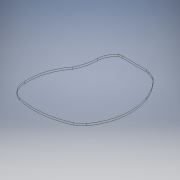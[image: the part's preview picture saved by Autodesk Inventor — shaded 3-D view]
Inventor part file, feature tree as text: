
AUTODESK INVENTOR PART (.ipt)
format: ipt  version: 2018 (Build 220112000, 112)  size: 170,496 bytes
history: native  units: in
note: dims shown in document units (in); Inventor stores cm internally (conversion verified against a paired STEP export)
features: fillet x5, extrude x2, sketch x2, imported_body x1
ambient origin geometry x8: Origin, YZ Plane, XZ Plane, XY Plane, X Axis, Y Axis, Z Axis, Center Point
bodies: Solid1 (feature_tree)
feature tree (10):
  imported_body  "Base1"
  extrude  "Extrusion1"  Depth=0.0197in
  fillet  "Fillet1"  Radius=0.0394in
  fillet  "Fillet2"  Radius=0.0394in
  fillet  "Fillet3"  Radius=0.0787in
  fillet  "Fillet4"  Radius=0.3937in
  extrude  "Extrusion2"  [1 undecoded]
  fillet  "Fillet5"  [1 undecoded]
  sketch  "Sketch1"  dims[d0=0.3937in d1=0.0in d2=0.0197in d3=0.0394in d4=0.0394in d5=0.0787in d6=0.3937in d7=0.0in]
  sketch  "Sketch2"  dims[d8=0.0787in]
note: 2 required parameter values undecoded (feature->parameter linkage not recoverable at this tier; creation-order binding heuristic only, values carry confidence <= 0.55)
